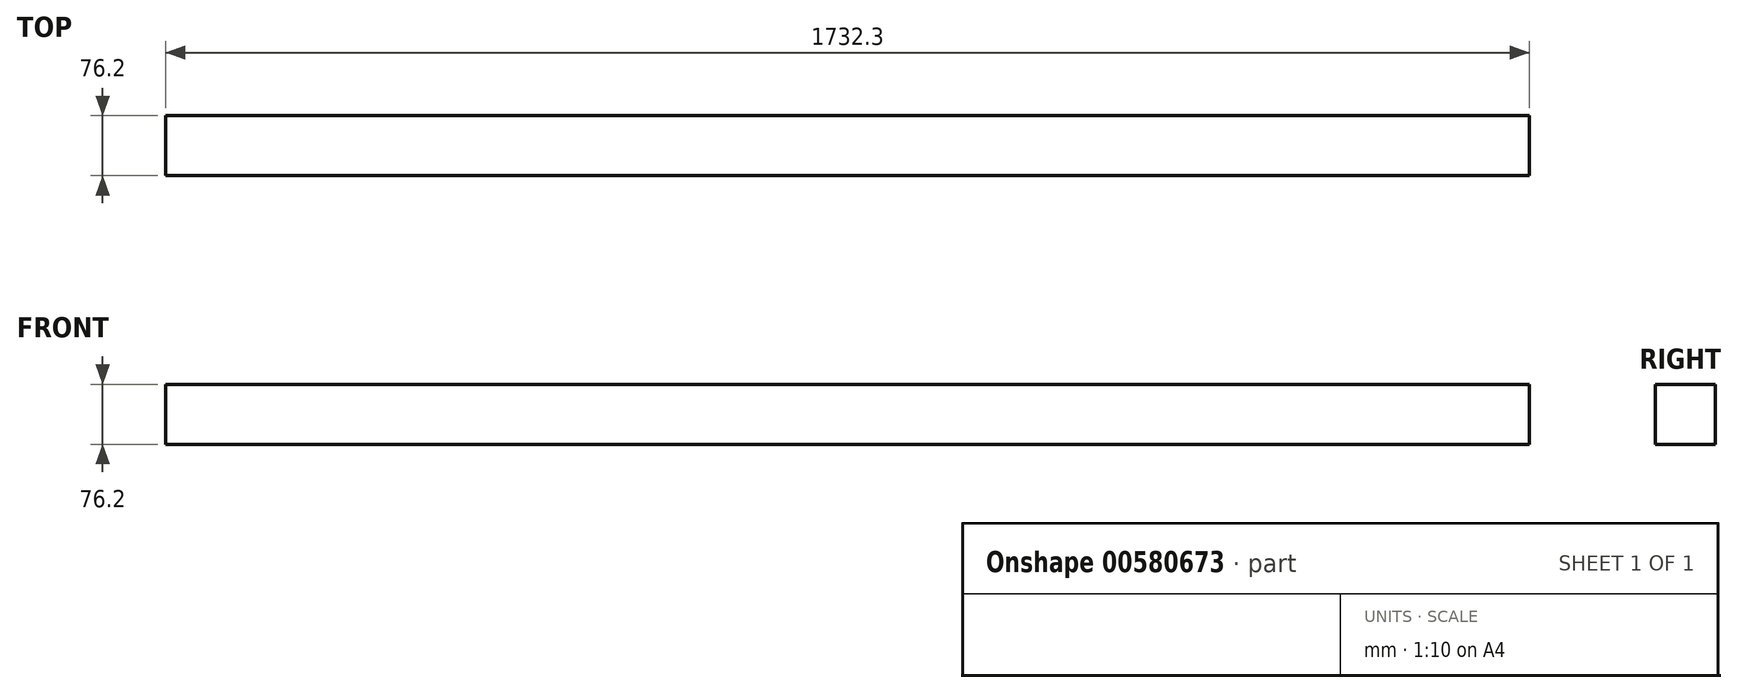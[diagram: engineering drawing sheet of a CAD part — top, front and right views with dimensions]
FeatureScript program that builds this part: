
annotation { "Feature Type Name" : "Feature", "Feature Type Description" : "" }
export const myFeature = defineFeature(function(context is Context, id is Id, definition is map)
    precondition{}
    {
        {
            var Q0;
            Q0=qCreatedBy(makeId("Top.planeOp"),FACE);
            var sketch = newSketch(context, id + "F0", { "sketchPlane" : qUnion([Q0])});
            skLineSegment(sketch, "E0.bottom", {"start": v(866.15, -38.1) * mm, "end": v(-866.15, -38.1) * mm});
            skLineSegment(sketch, "E0.top", {"start": v(866.15, 38.1) * mm, "end": v(-866.15, 38.1) * mm});
            skLineSegment(sketch, "E0.left", {"start": v(866.15, -38.1) * mm, "end": v(866.15, 38.1) * mm});
            skLineSegment(sketch, "E0.right", {"start": v(-866.15, -38.1) * mm, "end": v(-866.15, 38.1) * mm});
            skPoint(sketch, "E0.middle", {"position": v(0, 0) * mm});
            skSolve(sketch);
        }
        {
            var Q0;
            Q0=makeQuery(id+"F0.imprint","IMPRINT",FACE,{"disambiguationData":[TD([[makeQuery(id+"F0.imprint","IMPRINT",EDGE,{"derivedFrom":sQuery(id+"F0.wireOp",EDGE,"E0.bottom")}),-1.0]])]});
            extrude(context, id + "F1", {"entities" : qUnion([Q0]), "depth" : 76.2 * mm, "offsetDistance" : 25.4 * mm});
        }
    });
